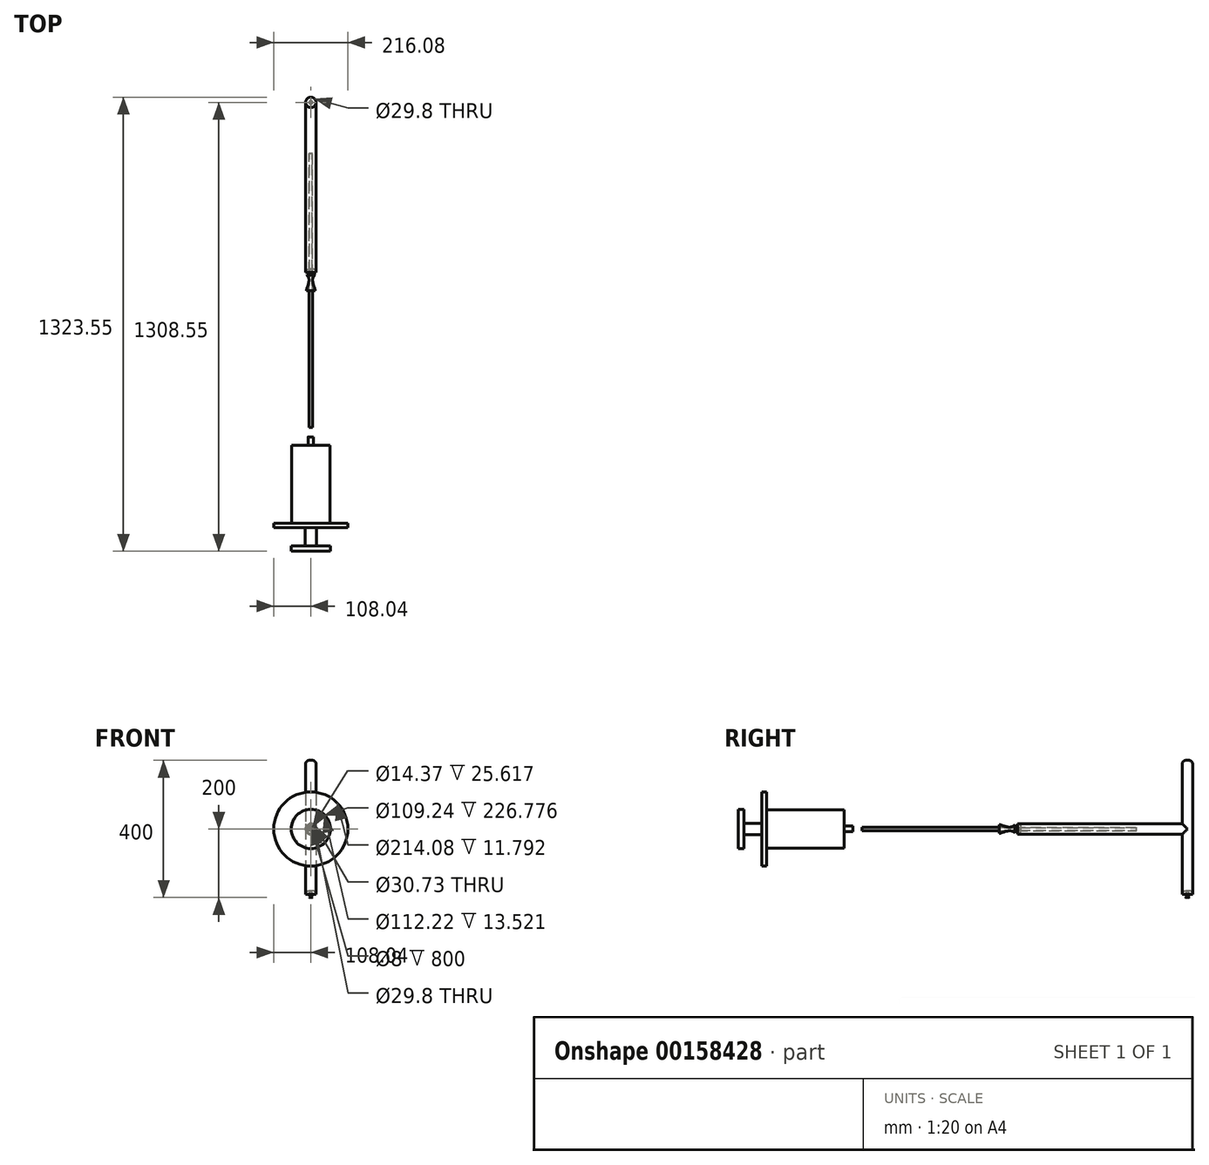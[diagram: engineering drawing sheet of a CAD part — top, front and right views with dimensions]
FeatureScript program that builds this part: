
annotation { "Feature Type Name" : "Feature", "Feature Type Description" : "" }
export const myFeature = defineFeature(function(context is Context, id is Id, definition is map)
    precondition{}
    {
        {
            var Q0;
            Q0=qCreatedBy(makeId("Top.planeOp"),FACE);
            var sketch = newSketch(context, id + "F0", { "sketchPlane" : qUnion([Q0])});
            skCircle(sketch, "E0", {"center": v(0, 0) * mm, "radius": 15 * mm});
            skSolve(sketch);
        }
        {
            var Q0;
            Q0=makeQuery(id+"F0.imprint","IMPRINT",FACE,{"disambiguationData":[TD([[makeQuery(id+"F0.imprint","IMPRINT",EDGE,{"derivedFrom":sQuery(id+"F0.wireOp",EDGE,"E0")}),1.0]])]});
            extrude(context, id + "F1", {"entities" : qUnion([Q0]), "endBound" : BoundingType.SYMMETRIC, "depth" : 400 * mm});
        }
        {
            var Q0;
            Q0=qCreatedBy(makeId("Front.planeOp"),FACE);
            var sketch = newSketch(context, id + "F2", { "sketchPlane" : qUnion([Q0])});
            skCircle(sketch, "E1", {"center": v(0, 0) * mm, "radius": 15 * mm});
            skSolve(sketch);
        }
        {
            var Q0;
            Q0 = qSketchRegion(id + "F2", true);
            extrude(context, id + "F3", {"entities" : qUnion([Q0]), "operationType" : NewBodyOperationType.ADD, "depth" : 500 * mm});
        }
        {
            var Q0;
            Q0=makeQuery(id+"F1.opExtrude","CAP_EDGE",EDGE,{"disambiguationData":[OSD([sQuery(id+"F0.wireOp",EDGE,"E0")])],"isStart":false});
            var Q1;
            Q1=makeQuery(id+"F1.opExtrude","CAP_EDGE",EDGE,{"disambiguationData":[OSD([sQuery(id+"F0.wireOp",EDGE,"E0")])],"isStart":true});
            fillet(context, id + "F4", {"entities" : qUnion([Q0, Q1]), "radius" : 10 * mm, "tangentPropagation" : true, "allowEdgeOverflow" : false});
        }
        {
            var Q0;
            Q0=qCreatedBy(makeId("Right.planeOp"),FACE);
            var sketch = newSketch(context, id + "F5", { "sketchPlane" : qUnion([Q0])});
            skLineSegment(sketch, "E2.0", {"start": v(-500, -15) * mm, "end": v(-500, 15) * mm});
            skFitSpline(sketch, "E3", {"points": [v(-500, -15) * mm, v(-524.47, -6) * mm, v(-560.23, -15) * mm, v(-560.23, 0) * mm], "startDerivative": vector(-59.25, 72.79) * mm, "endDerivative": vector(-9.37, 82.85) * mm});
            skLineSegment(sketch, "E4", {"start": v(-500, 0) * mm, "end": v(-548.33, 0) * mm, "construction": true});
            skPoint(sketch, "E4.endSnap0", {"position": v(-500, 0) * mm});
            skLineSegment(sketch, "E5", {"start": v(-548.33, 0) * mm, "end": v(-500, 0) * mm});
            skLineSegment(sketch, "E6", {"start": v(-548.33, -13.18) * mm, "end": v(-548.33, 0) * mm});
            skSolve(sketch);
        }
        {
            var Q0;
            {var subQ0=sQuery(id+"F5.wireOp",EDGE,"E3");Q0=makeQuery(id+"F5.imprint","IMPRINT",FACE,{"disambiguationData":[TD([[makeQuery(id+"F5.imprint","IMPRINT",EDGE,{"derivedFrom":subQ0}),-1.0]])]});}
            var Q1;
            Q1=sQuery(id+"F5.wireOp",EDGE,"E5");
            revolve(context, id + "F6", {"operationType" : NewBodyOperationType.ADD, "entities" : qUnion([Q0]), "axis" : qUnion([Q1]), "revolveType" : RevolveType.FULL});
        }
        {
            var Q0;
            Q0=makeQuery(id+"F6.boolean.opBoolean","MERGE",EDGE,{"derivedFrom":[makeQuery(id+"F3.opExtrude","CAP_EDGE",EDGE,{"disambiguationData":[OSD([sQuery(id+"F2.wireOp",EDGE,"E1")])],"isStart":false}),makeQuery(id+"F6.opRevolve","SWEPT_EDGE",EDGE,{"disambiguationData":[OSD([sQuery(id+"F5.wireOp",EDGE,"E2.0"),sQuery(id+"F5.wireOp",EDGE,"E3")])]})]});
            fillet(context, id + "F7", {"entities" : qUnion([Q0]), "radius" : 10 * mm, "tangentPropagation" : true, "allowEdgeOverflow" : false});
        }
        {
            var Q0;
            Q0=makeQuery(id+"F6.opRevolve","SWEPT_FACE",FACE,{"disambiguationData":[OSD([sQuery(id+"F5.wireOp",EDGE,"E6")])]});
            var sketch = newSketch(context, id + "F8", { "sketchPlane" : qUnion([Q0])});
            skCircle(sketch, "E7", {"center": v(0, 0) * mm, "radius": 5 * mm});
            skCircle(sketch, "E8", {"center": v(0, 0) * mm, "radius": 4 * mm});
            skSolve(sketch);
        }
        {
            var Q0;
            Q0=makeQuery(id+"F6.opRevolve","SWEPT_FACE",FACE,{"disambiguationData":[OSD([sQuery(id+"F5.wireOp",EDGE,"E6")])]});
            shell(context, id + "F9", {"entities" : qUnion([Q0]), "thickness" : 0.1 * mm});
        }
        {
            var Q0;
            Q0=makeQuery(id+"F8.imprint","IMPRINT",FACE,{"disambiguationData":[TD([[makeQuery(id+"F8.imprint","IMPRINT",EDGE,{"derivedFrom":sQuery(id+"F8.wireOp",EDGE,"E7")}),1.0]])]});
            extrude(context, id + "F10", {"entities" : qUnion([Q0]), "endBound" : BoundingType.SYMMETRIC, "depth" : 800 * mm});
        }
        {
            var Q0;
            Q0=qCreatedBy(makeId("Right.planeOp"),FACE);
            var sketch = newSketch(context, id + "F11", { "sketchPlane" : qUnion([Q0])});
            skLineSegment(sketch, "E9.0", {"start": v(-948.33, -5) * mm, "end": v(-948.33, 5) * mm});
            skLineSegment(sketch, "E10.bottom", {"start": v(-975.26, 0) * mm, "end": v(-999.88, 0) * mm});
            skLineSegment(sketch, "E10.top", {"start": v(-975.26, 8.18) * mm, "end": v(-999.88, 8.18) * mm});
            skLineSegment(sketch, "E10.left", {"start": v(-975.26, 0) * mm, "end": v(-975.26, 8.18) * mm});
            skLineSegment(sketch, "E10.right", {"start": v(-999.88, 0) * mm, "end": v(-999.88, 8.18) * mm});
            skLineSegment(sketch, "E11.bottom", {"start": v(-999.88, 0) * mm, "end": v(-1226.66, 0) * mm});
            skLineSegment(sketch, "E11.top", {"start": v(-999.88, 55.62) * mm, "end": v(-1226.66, 55.62) * mm});
            skLineSegment(sketch, "E11.left", {"start": v(-999.88, 0) * mm, "end": v(-999.88, 55.62) * mm});
            skLineSegment(sketch, "E11.right", {"start": v(-1226.66, 0) * mm, "end": v(-1226.66, 55.62) * mm});
            skLineSegment(sketch, "E12.bottom", {"start": v(-1226.66, 0) * mm, "end": v(-1240.45, 0) * mm});
            skLineSegment(sketch, "E12.top", {"start": v(-1226.66, 108.04) * mm, "end": v(-1240.45, 108.04) * mm});
            skLineSegment(sketch, "E12.left", {"start": v(-1226.66, 0) * mm, "end": v(-1226.66, 108.04) * mm});
            skLineSegment(sketch, "E12.right", {"start": v(-1240.45, 0) * mm, "end": v(-1240.45, 108.04) * mm});
            skLineSegment(sketch, "E13.bottom", {"start": v(-1240.45, 0) * mm, "end": v(-1293.03, 0) * mm});
            skLineSegment(sketch, "E13.top", {"start": v(-1240.45, 16.37) * mm, "end": v(-1293.03, 16.37) * mm});
            skLineSegment(sketch, "E13.left", {"start": v(-1240.45, 0) * mm, "end": v(-1240.45, 16.37) * mm});
            skLineSegment(sketch, "E13.right", {"start": v(-1293.03, 0) * mm, "end": v(-1293.03, 16.37) * mm});
            skLineSegment(sketch, "E14.bottom", {"start": v(-1293.03, 0) * mm, "end": v(-1308.55, 0) * mm});
            skLineSegment(sketch, "E14.top", {"start": v(-1293.03, 57.11) * mm, "end": v(-1308.55, 57.11) * mm});
            skLineSegment(sketch, "E14.left", {"start": v(-1293.03, 0) * mm, "end": v(-1293.03, 57.11) * mm});
            skLineSegment(sketch, "E14.right", {"start": v(-1308.55, 0) * mm, "end": v(-1308.55, 57.11) * mm});
            skSolve(sketch);
        }
        {
            var Q0;
            {var subQ1=sQuery(id+"F11.wireOp",EDGE,"E11.bottom");Q0=makeQuery(id+"F11.imprint","IMPRINT",FACE,{"disambiguationData":[TD([[makeQuery(id+"F11.imprint","IMPRINT",EDGE,{"derivedFrom":subQ1}),-1.0]])]});}
            var Q1;
            {var subQ0=sQuery(id+"F11.wireOp",EDGE,"E10.bottom");Q1=makeQuery(id+"F11.imprint","IMPRINT",FACE,{"disambiguationData":[TD([[makeQuery(id+"F11.imprint","IMPRINT",EDGE,{"derivedFrom":subQ0}),-1.0]])]});}
            var Q2;
            {var subQ0=sQuery(id+"F11.wireOp",EDGE,"E13.bottom");Q2=makeQuery(id+"F11.imprint","IMPRINT",FACE,{"disambiguationData":[TD([[makeQuery(id+"F11.imprint","IMPRINT",EDGE,{"derivedFrom":subQ0}),-1.0]])]});}
            var Q3;
            {var subQ1=sQuery(id+"F11.wireOp",EDGE,"E12.bottom");Q3=makeQuery(id+"F11.imprint","IMPRINT",FACE,{"disambiguationData":[TD([[makeQuery(id+"F11.imprint","IMPRINT",EDGE,{"derivedFrom":subQ1}),-1.0]])]});}
            var Q4;
            {var subQ3=sQuery(id+"F11.wireOp",EDGE,"E14.bottom");Q4=makeQuery(id+"F11.imprint","IMPRINT",FACE,{"disambiguationData":[TD([[makeQuery(id+"F11.imprint","IMPRINT",EDGE,{"derivedFrom":subQ3}),-1.0]])]});}
            var Q5;
            Q5=sQuery(id+"F11.wireOp",EDGE,"E11.bottom");
            revolve(context, id + "F12", {"entities" : qUnion([Q0, Q1, Q2, Q3, Q4]), "axis" : qUnion([Q5]), "revolveType" : RevolveType.FULL});
        }
        {
            var Q0;
            Q0=makeQuery(id+"F12.opRevolve","SWEPT_FACE",FACE,{"disambiguationData":[OSD([sQuery(id+"F11.wireOp",EDGE,"E10.left")])]});
            shell(context, id + "F13", {"entities" : qUnion([Q0]), "thickness" : 1 * mm});
        }
    });
